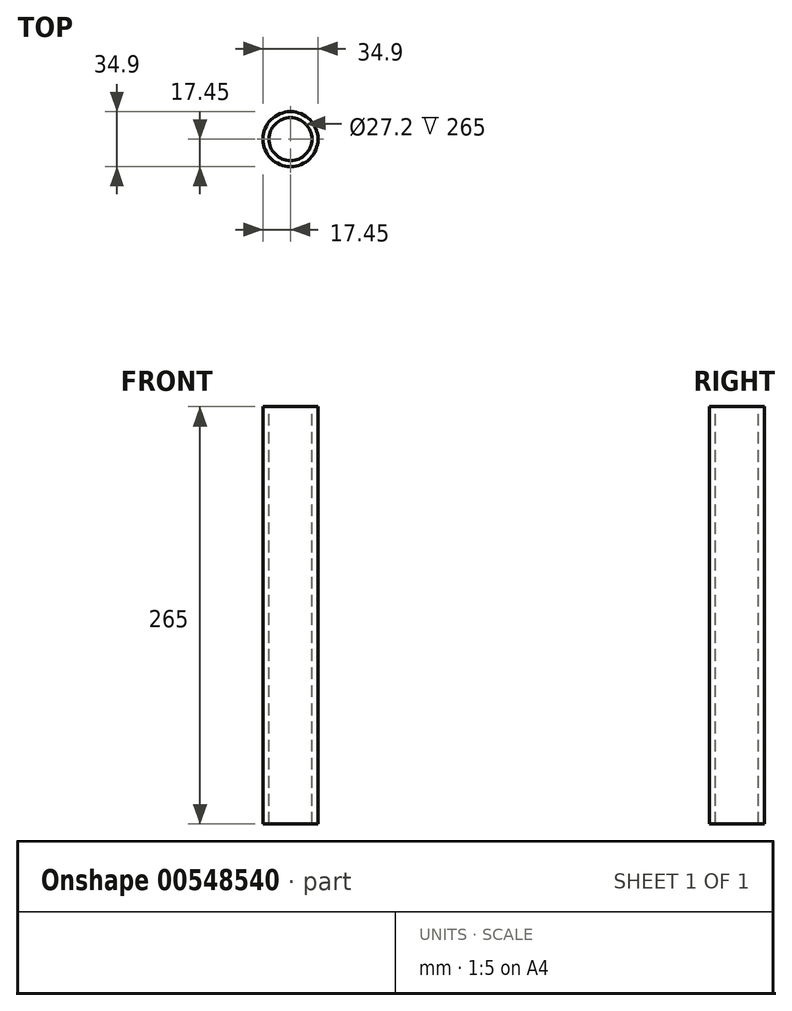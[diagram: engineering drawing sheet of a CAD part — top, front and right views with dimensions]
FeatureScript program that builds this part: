
annotation { "Feature Type Name" : "Feature", "Feature Type Description" : "" }
export const myFeature = defineFeature(function(context is Context, id is Id, definition is map)
    precondition{}
    {
        {
            var Q0;
            Q0=qCreatedBy(makeId("Top.planeOp"),FACE);
            var sketch = newSketch(context, id + "F0", { "sketchPlane" : qUnion([Q0])});
            skCircle(sketch, "E0", {"center": v(0, 0) * mm, "radius": 17.45 * mm});
            skCircle(sketch, "E1", {"center": v(0, 0) * mm, "radius": 13.6 * mm});
            skSolve(sketch);
        }
        {
            var Q0;
            Q0=makeQuery(id+"F0.imprint","IMPRINT",FACE,{"disambiguationData":[TD([[makeQuery(id+"F0.imprint","IMPRINT",EDGE,{"derivedFrom":sQuery(id+"F0.wireOp",EDGE,"E0")}),1.0]])]});
            extrude(context, id + "F1", {"entities" : qUnion([Q0]), "oppositeDirection" : true, "depth" : 265 * mm, "offsetDistance" : 25.4 * mm});
        }
    });
